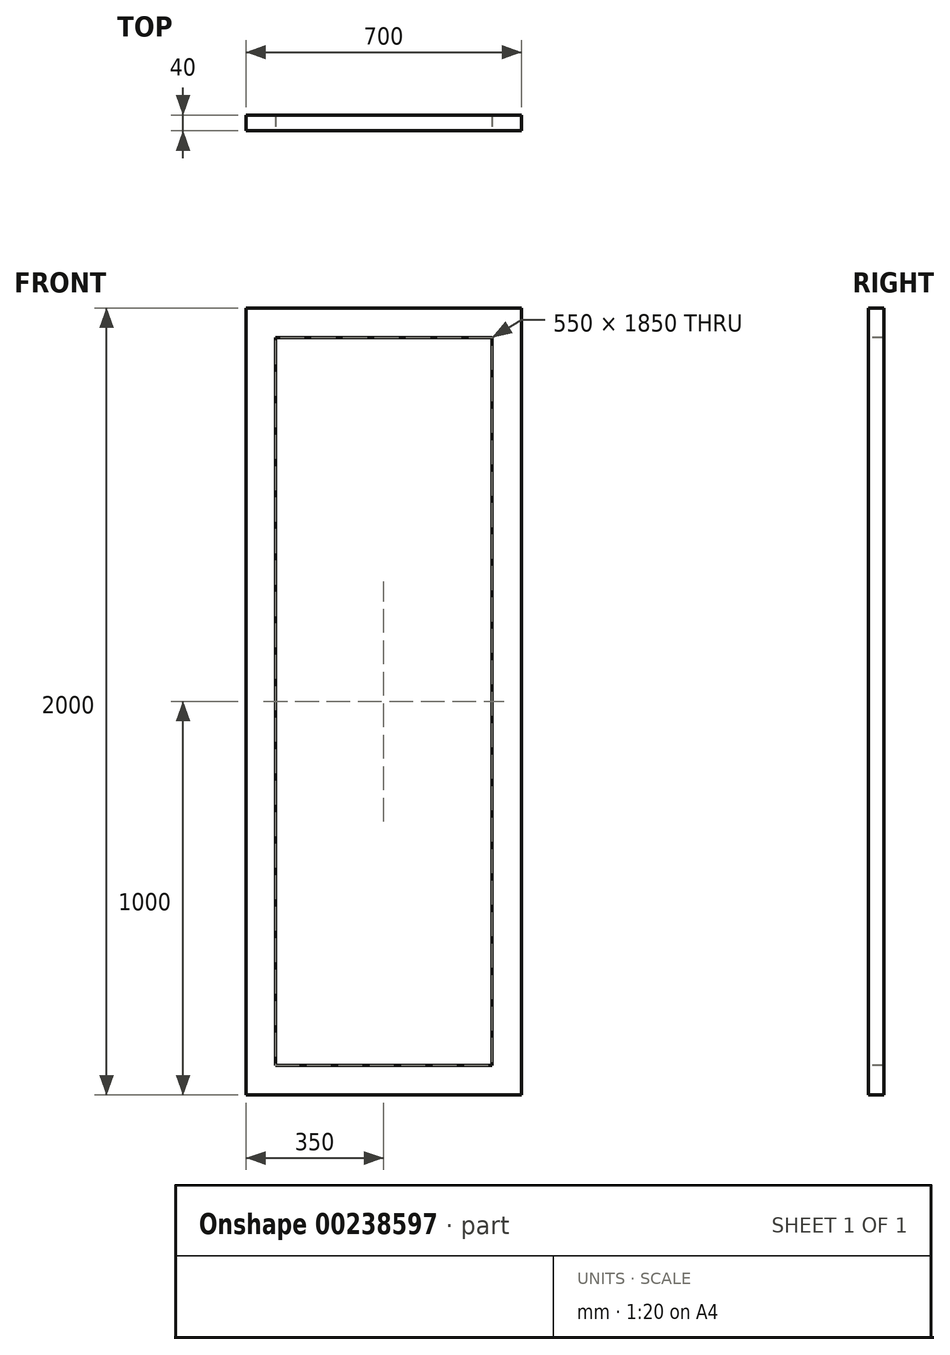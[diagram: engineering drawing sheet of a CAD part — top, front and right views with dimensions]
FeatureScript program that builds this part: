
annotation { "Feature Type Name" : "Feature", "Feature Type Description" : "" }
export const myFeature = defineFeature(function(context is Context, id is Id, definition is map)
    precondition{}
    {
        {
            var Q0;
            Q0=qCreatedBy(makeId("Front.planeOp"),FACE);
            var sketch = newSketch(context, id + "F0", { "sketchPlane" : qUnion([Q0])});
            skLineSegment(sketch, "E0.bottom", {"start": v(350, -1000) * mm, "end": v(-350, -1000) * mm});
            skLineSegment(sketch, "E0.top", {"start": v(350, 1000) * mm, "end": v(-350, 1000) * mm});
            skLineSegment(sketch, "E0.left", {"start": v(350, -1000) * mm, "end": v(350, 1000) * mm});
            skLineSegment(sketch, "E0.right", {"start": v(-350, -1000) * mm, "end": v(-350, 1000) * mm});
            skPoint(sketch, "E0.middle", {"position": v(0, 0) * mm});
            skSolve(sketch);
        }
        {
            var Q0;
            Q0=makeQuery(id+"F0.imprint","IMPRINT",FACE,{"disambiguationData":[TD([[makeQuery(id+"F0.imprint","IMPRINT",EDGE,{"derivedFrom":sQuery(id+"F0.wireOp",EDGE,"E0.bottom")}),-1.0]])]});
            extrude(context, id + "F1", {"entities" : qUnion([Q0]), "depth" : 40 * mm});
        }
        {
            var Q0;
            Q0=makeQuery(id+"F1.opExtrude","CAP_FACE",FACE,{"disambiguationData":[OSD([sQuery(id+"F0.wireOp",EDGE,"E0.bottom"),sQuery(id+"F0.wireOp",EDGE,"E0.top"),sQuery(id+"F0.wireOp",EDGE,"E0.left"),sQuery(id+"F0.wireOp",EDGE,"E0.right")])],"isStart":false});
            var sketch = newSketch(context, id + "F2", { "sketchPlane" : qUnion([Q0])});
            skLineSegment(sketch, "E1.bottom", {"start": v(-275, 925) * mm, "end": v(275, 925) * mm});
            skLineSegment(sketch, "E1.top", {"start": v(-275, -925) * mm, "end": v(275, -925) * mm});
            skLineSegment(sketch, "E1.left", {"start": v(-275, 925) * mm, "end": v(-275, -925) * mm});
            skLineSegment(sketch, "E1.right", {"start": v(275, 925) * mm, "end": v(275, -925) * mm});
            skPoint(sketch, "E1.middle", {"position": v(0, 0) * mm});
            skSolve(sketch);
        }
        {
            var Q0;
            Q0 = qSketchRegion(id + "F2", true);
            var Q1;
            Q1=sQuery(id+"F2.wireOp",EDGE,"E1.bottom");
            extrude(context, id + "F3", {"entities" : qUnion([Q0]), "operationType" : NewBodyOperationType.REMOVE, "surfaceEntities" : qUnion([Q1]), "endBound" : BoundingType.THROUGH_ALL, "oppositeDirection" : true, "depth" : 25 * mm});
        }
    });
